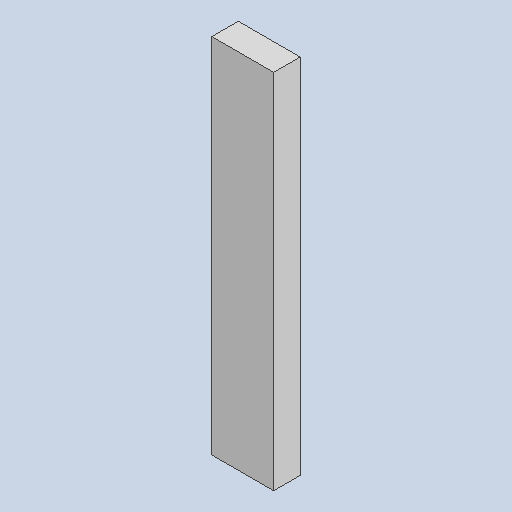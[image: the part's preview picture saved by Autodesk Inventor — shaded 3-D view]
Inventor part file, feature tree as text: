
AUTODESK INVENTOR PART (.ipt)
format: ipt  version: 2025 (Build 290162000, 162)  size: 79,360 bytes
history: native  units: in
note: dims shown in document units (in); Inventor stores cm internally (conversion verified against a paired STEP export)
features: other x3, sketch x1
ambient origin geometry x8: Origin, YZ Plane, XZ Plane, XY Plane, X Axis, Y Axis, Z Axis, Center Point
bodies: Solid1 (feature_tree)
feature tree (4):
  other  "side-side2.ipt"
  other  "Solid1::side-side2.ipt"
  other  "TaggingFeature1"
  sketch  "Sketch1"  dims[d0=0.3937in]
